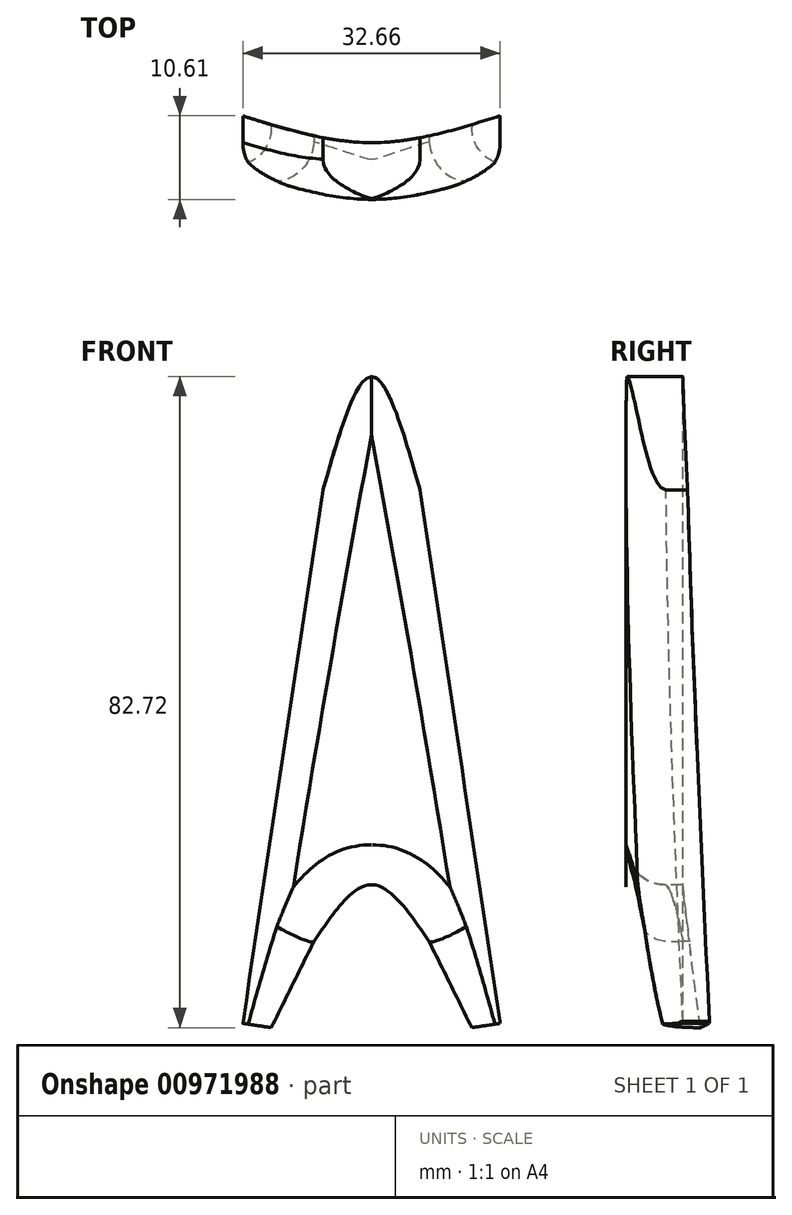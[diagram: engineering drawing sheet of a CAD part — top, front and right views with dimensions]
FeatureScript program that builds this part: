
annotation { "Feature Type Name" : "Feature", "Feature Type Description" : "" }
export const myFeature = defineFeature(function(context is Context, id is Id, definition is map)
    precondition{}
    {
        {
            var Q0;
            Q0=qCreatedBy(makeId("Front.planeOp"),FACE);
            var sketch = newSketch(context, id + "F0", { "sketchPlane" : qUnion([Q0])});
            skLineSegment(sketch, "E0", {"start": v(-10.17, -14.44) * mm, "end": v(-20.35, -82.18) * mm});
            skLineSegment(sketch, "E1", {"start": v(-20.35, -82.18) * mm, "end": v(-16.74, -82.72) * mm});
            skLineSegment(sketch, "E2", {"start": v(-16.74, -82.72) * mm, "end": v(-11.3, -71.74) * mm});
            skLineSegment(sketch, "E3", {"start": v(-4, 0) * mm, "end": v(-4, -85.17) * mm});
            skLineSegment(sketch, "E4.MirrorCS", {"start": v(2.17, -14.44) * mm, "end": v(12.35, -82.18) * mm});
            skLineSegment(sketch, "E5.MirrorCS", {"start": v(12.35, -82.18) * mm, "end": v(8.74, -82.72) * mm});
            skLineSegment(sketch, "E6.MirrorCS", {"start": v(8.74, -82.72) * mm, "end": v(3.3, -71.74) * mm});
            skFitSpline(sketch, "E7", {"points": [v(-11.3, -71.74) * mm, v(-4, -64.57) * mm, v(3.3, -71.74) * mm], "startDerivative": vector(14.6, 21.53) * mm, "endDerivative": vector(14.6, -21.53) * mm});
            skFitSpline(sketch, "E8", {"points": [v(-10.17, -14.44) * mm, v(-4, 0) * mm, v(2.17, -14.44) * mm], "startDerivative": vector(12.34, 43.31) * mm, "endDerivative": vector(12.34, -43.31) * mm});
            skLineSegment(sketch, "E9", {"start": v(-35.23, 23.08) * mm, "end": v(-35.23, -109.15) * mm});
            skLineSegment(sketch, "E10", {"start": v(37.56, -109.15) * mm, "end": v(37.56, 32.52) * mm});
            skLineSegment(sketch, "E11", {"start": v(37.56, 32.52) * mm, "end": v(-35.23, 23.08) * mm});
            skLineSegment(sketch, "E12", {"start": v(-35.23, -109.15) * mm, "end": v(37.56, -109.15) * mm});
            skSolve(sketch);
        }
        {
            var Q0;
            Q0=qCreatedBy(makeId("Top.planeOp"),FACE);
            var sketch = newSketch(context, id + "F1", { "sketchPlane" : qUnion([Q0])});
            skFitSpline(sketch, "E13", {"points": [v(-20.38, 7.11) * mm, v(-3.9, 3.6) * mm, v(12.3, 7.11) * mm], "startDerivative": vector(32.9, -10.5) * mm, "endDerivative": vector(32.49, 10.53) * mm});
            skLineSegment(sketch, "E14", {"start": v(12.3, 7.11) * mm, "end": v(12.3, 14.22) * mm});
            skLineSegment(sketch, "E15", {"start": v(-20.38, 7.11) * mm, "end": v(-20.38, 14.22) * mm});
            skLineSegment(sketch, "E16", {"start": v(-3.9, 3.6) * mm, "end": v(-3.9, 10.82) * mm});
            skFitSpline(sketch, "E17", {"points": [v(-20.38, 14.22) * mm, v(-3.9, 10.82) * mm, v(12.3, 14.22) * mm], "startDerivative": vector(32.9, -10.2) * mm, "endDerivative": vector(32.49, 10.23) * mm});
            skSolve(sketch);
        }
        {
            var Q0;
            {var subQ0=sQuery(id+"F1.wireOp",EDGE,"E15");Q0=makeQuery(id+"F1.imprint","IMPRINT",FACE,{"disambiguationData":[TD([[makeQuery(id+"F1.imprint","IMPRINT",EDGE,{"derivedFrom":subQ0}),-1.0]])]});}
            var Q1;
            {var subQ0=sQuery(id+"F1.wireOp",EDGE,"E14");Q1=makeQuery(id+"F1.imprint","IMPRINT",FACE,{"disambiguationData":[TD([[makeQuery(id+"F1.imprint","IMPRINT",EDGE,{"derivedFrom":subQ0}),1.0]])]});}
            extrude(context, id + "F2", {"entities" : qUnion([Q0, Q1]), "oppositeDirection" : true, "depth" : 83.06 * mm, "offsetDistance" : 25.4 * mm});
        }
        {
            var Q0;
            {var subQ4=sQuery(id+"F0.wireOp",EDGE,"E0");Q0=makeQuery(id+"F0.imprint","IMPRINT",FACE,{"disambiguationData":[TD([[makeQuery(id+"F0.imprint","IMPRINT",EDGE,{"derivedFrom":subQ4}),-1.0]])]});}
            extrude(context, id + "F3", {"entities" : qUnion([Q0]), "operationType" : NewBodyOperationType.REMOVE, "oppositeDirection" : true, "depth" : 24.9 * mm, "offsetDistance" : 25.4 * mm});
        }
        {
            var Q0;
            Q0=makeQuery(id+"F3.boolean.opBoolean","INTERSECT",EDGE,{"derivedFrom":[makeQuery(id+"F2.opExtrude","SWEPT_FACE",FACE,{"disambiguationData":[OSD([sQuery(id+"F1.wireOp",EDGE,"E13")])]}),makeQuery(id+"F3.opExtrude","SWEPT_FACE",FACE,{"disambiguationData":[OSD([sQuery(id+"F0.wireOp",EDGE,"E4.MirrorCS")])]})]});
            var Q1;
            Q1=makeQuery(id+"F3.boolean.opBoolean","INTERSECT",EDGE,{"derivedFrom":[makeQuery(id+"F2.opExtrude","SWEPT_FACE",FACE,{"disambiguationData":[OSD([sQuery(id+"F1.wireOp",EDGE,"E13")])]}),makeQuery(id+"F3.opExtrude","SWEPT_FACE",FACE,{"disambiguationData":[OSD([sQuery(id+"F0.wireOp",EDGE,"E0")])]})]});
            var Q2;
            Q2=makeQuery(id+"F3.boolean.opBoolean","INTERSECT",EDGE,{"derivedFrom":[makeQuery(id+"F2.opExtrude","SWEPT_FACE",FACE,{"disambiguationData":[OSD([sQuery(id+"F1.wireOp",EDGE,"E13")])]}),makeQuery(id+"F3.opExtrude","SWEPT_FACE",FACE,{"disambiguationData":[OSD([sQuery(id+"F0.wireOp",EDGE,"E7")])]})]});
            var Q3;
            Q3=makeQuery(id+"F3.boolean.opBoolean","INTERSECT",EDGE,{"derivedFrom":[makeQuery(id+"F2.opExtrude","SWEPT_FACE",FACE,{"disambiguationData":[OSD([sQuery(id+"F1.wireOp",EDGE,"E13")])]}),makeQuery(id+"F3.opExtrude","SWEPT_FACE",FACE,{"disambiguationData":[OSD([sQuery(id+"F0.wireOp",EDGE,"E6.MirrorCS")])]})]});
            var Q4;
            Q4=makeQuery(id+"F3.boolean.opBoolean","INTERSECT",EDGE,{"derivedFrom":[makeQuery(id+"F2.opExtrude","SWEPT_FACE",FACE,{"disambiguationData":[OSD([sQuery(id+"F1.wireOp",EDGE,"E13")])]}),makeQuery(id+"F3.opExtrude","SWEPT_FACE",FACE,{"disambiguationData":[OSD([sQuery(id+"F0.wireOp",EDGE,"E2")])]})]});
            fillet(context, id + "F4", {"entities" : qUnion([Q0, Q1, Q2, Q3, Q4]), "radius" : 5.08 * mm, "tangentPropagation" : true, "allowEdgeOverflow" : false});
        }
    });
